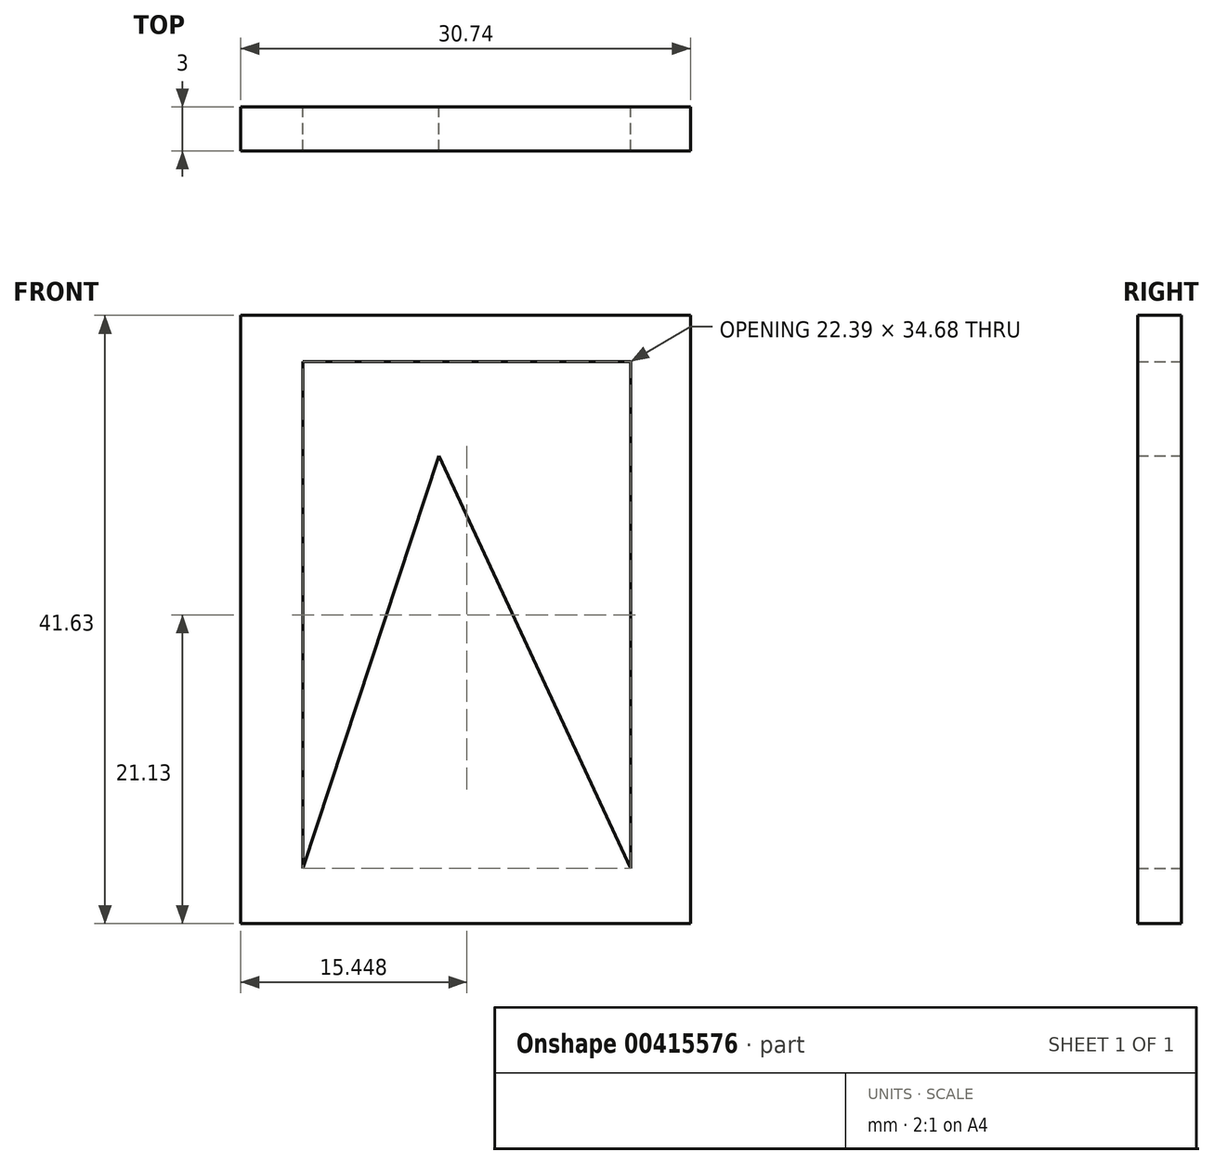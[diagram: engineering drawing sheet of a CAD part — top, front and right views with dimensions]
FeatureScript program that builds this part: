
annotation { "Feature Type Name" : "Feature", "Feature Type Description" : "" }
export const myFeature = defineFeature(function(context is Context, id is Id, definition is map)
    precondition{}
    {
        {
            var Q0;
            Q0=qCreatedBy(makeId("Front.planeOp"),FACE);
            var sketch = newSketch(context, id + "F0", { "sketchPlane" : qUnion([Q0])});
            skLineSegment(sketch, "E0", {"start": v(16.32, -11.11) * mm, "end": v(16.32, -52.74) * mm});
            skLineSegment(sketch, "E1", {"start": v(16.32, -52.74) * mm, "end": v(47.06, -52.74) * mm});
            skLineSegment(sketch, "E2", {"start": v(47.06, -52.74) * mm, "end": v(47.06, -11.11) * mm});
            skLineSegment(sketch, "E3", {"start": v(47.06, -11.11) * mm, "end": v(16.32, -11.11) * mm});
            skLineSegment(sketch, "E4", {"start": v(20.57, -14.27) * mm, "end": v(20.57, -48.95) * mm});
            skLineSegment(sketch, "E5", {"start": v(20.57, -48.95) * mm, "end": v(29.88, -20.73) * mm});
            skLineSegment(sketch, "E6", {"start": v(29.88, -20.73) * mm, "end": v(42.96, -48.95) * mm});
            skLineSegment(sketch, "E7", {"start": v(42.96, -48.95) * mm, "end": v(42.96, -14.27) * mm});
            skLineSegment(sketch, "E8", {"start": v(20.57, -14.27) * mm, "end": v(42.96, -14.27) * mm});
            skSolve(sketch);
        }
        {
            var Q0;
            Q0=makeQuery(id+"F0.imprint","IMPRINT",FACE,{"disambiguationData":[TD([[makeQuery(id+"F0.imprint","IMPRINT",EDGE,{"derivedFrom":sQuery(id+"F0.wireOp",EDGE,"E0")}),1.0]])]});
            extrude(context, id + "F1", {"entities" : qUnion([Q0]), "depth" : 3 * mm});
        }
    });
